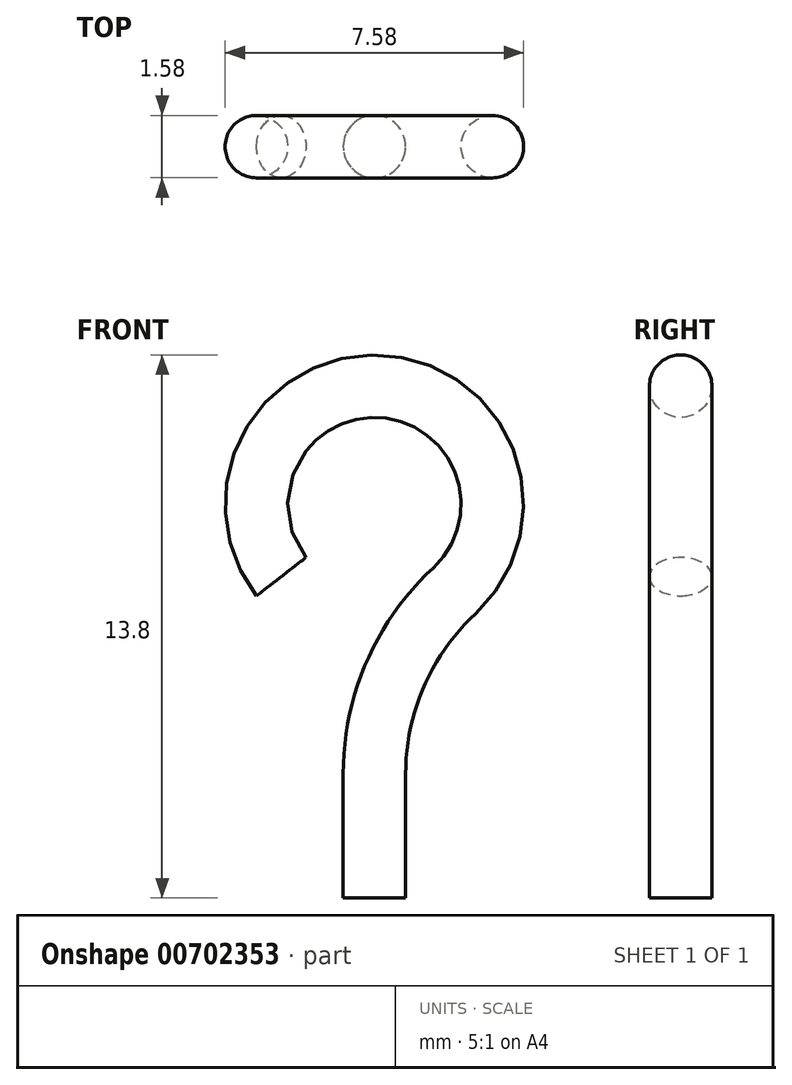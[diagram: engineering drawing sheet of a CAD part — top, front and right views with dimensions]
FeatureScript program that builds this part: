
annotation { "Feature Type Name" : "Feature", "Feature Type Description" : "" }
export const myFeature = defineFeature(function(context is Context, id is Id, definition is map)
    precondition{}
    {
        {
            var Q0;
            Q0=qCreatedBy(makeId("Front.planeOp"),FACE);
            var sketch = newSketch(context, id + "F0", { "sketchPlane" : qUnion([Q0])});
            skArc(sketch, "E0", {"start": v(2.04, 7.8) * mm, "mid": v(0.24, 13) * mm, "end": v(-2.36, 8.17) * mm});
            skLineSegment(sketch, "E1", {"start": v(0, 3.15) * mm, "end": v(0, 0) * mm});
            skLineSegment(sketch, "E2", {"start": v(0, 10) * mm, "end": v(-2.36, 8.17) * mm});
            skArc(sketch, "E3.filletArc", {"start": v(2.04, 7.8) * mm, "mid": v(0.53, 5.7) * mm, "end": v(0, 3.15) * mm});
            skSolve(sketch);
        }
        {
            var Q0;
            Q0=qCreatedBy(makeId("Top.planeOp"),FACE);
            var sketch = newSketch(context, id + "F1", { "sketchPlane" : qUnion([Q0])});
            skCircle(sketch, "E4", {"center": v(0, 0) * mm, "radius": 0.8 * mm});
            skSolve(sketch);
        }
        {
            var Q0;
            Q0=makeQuery(id+"F1.imprint","IMPRINT",FACE,{"disambiguationData":[TD([[makeQuery(id+"F1.imprint","IMPRINT",EDGE,{"derivedFrom":sQuery(id+"F1.wireOp",EDGE,"E4")}),1.0]])]});
            var Q1;
            Q1=sQuery(id+"F0.wireOp",EDGE,"E1");
            var Q2;
            Q2=sQuery(id+"F0.wireOp",EDGE,"E3.filletArc");
            var Q3;
            Q3=sQuery(id+"F0.wireOp",EDGE,"E0");
            sweep(context, id + "F2", {"profiles" : qUnion([Q0]), "path" : qUnion([Q1, Q2, Q3])});
        }
    });
